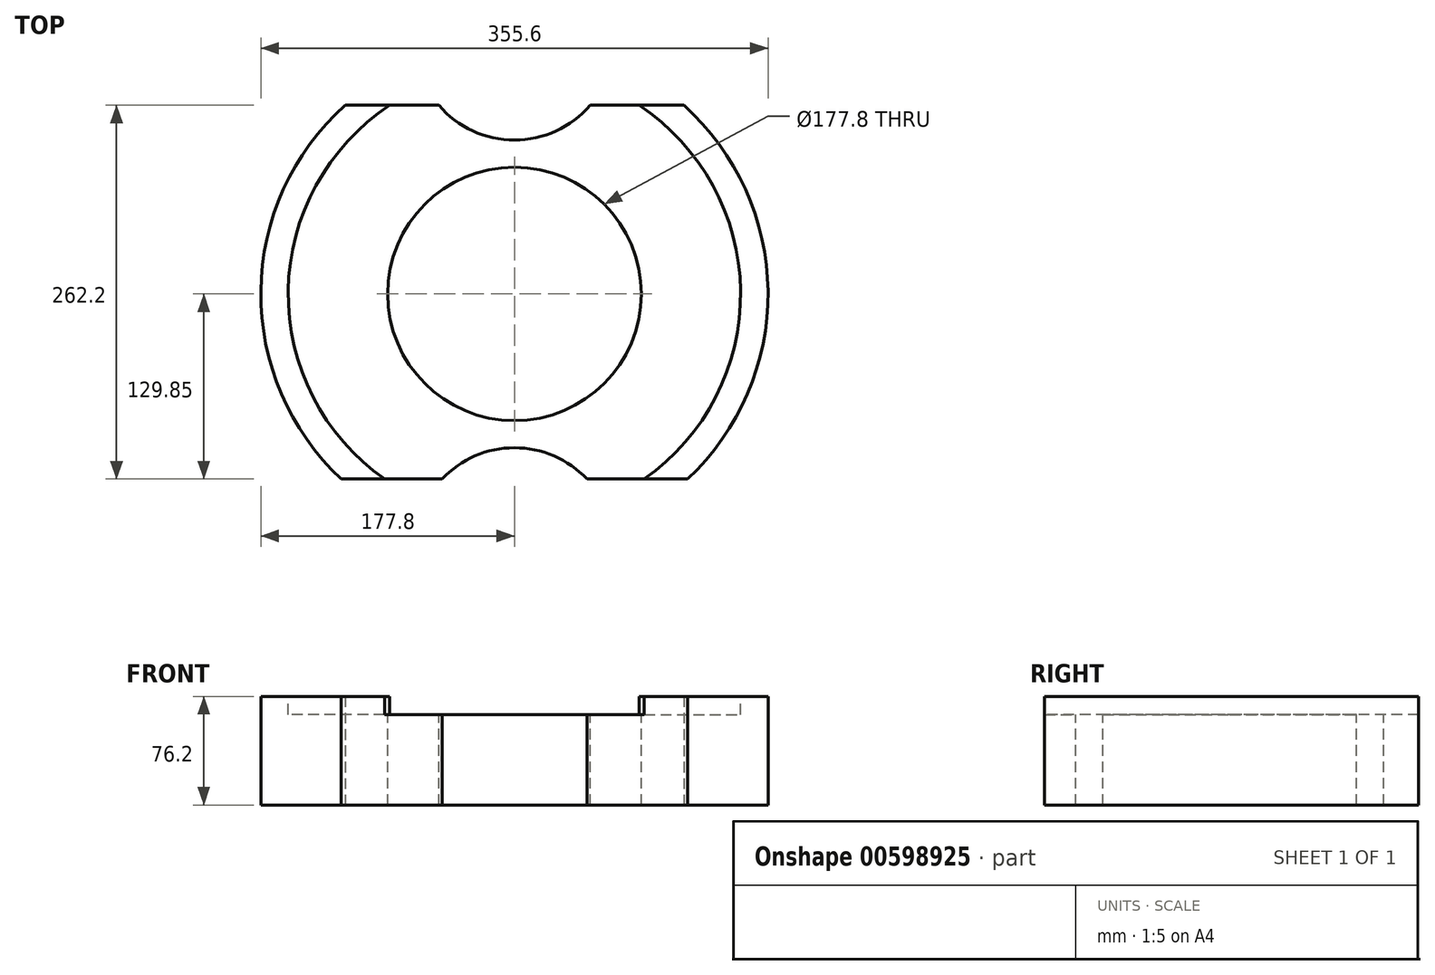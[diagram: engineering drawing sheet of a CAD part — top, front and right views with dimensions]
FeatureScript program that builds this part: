
annotation { "Feature Type Name" : "Feature", "Feature Type Description" : "" }
export const myFeature = defineFeature(function(context is Context, id is Id, definition is map)
    precondition{}
    {
        {
            var Q0;
            Q0=qCreatedBy(makeId("Top.planeOp"),FACE);
            var sketch = newSketch(context, id + "F0", { "sketchPlane" : qUnion([Q0])});
            skCircle(sketch, "E0", {"center": v(0, 0) * mm, "radius": 177.8 * mm});
            skSolve(sketch);
        }
        {
            var Q0;
            Q0 = qSketchRegion(id + "F0", true);
            extrude(context, id + "F1", {"entities" : qUnion([Q0]), "depth" : 76.2 * mm, "offsetDistance" : 25.4 * mm});
        }
        {
            var Q0;
            Q0=makeQuery(id+"F1.opExtrude","CAP_FACE",FACE,{"disambiguationData":[OSD([sQuery(id+"F0.wireOp",EDGE,"E0")])],"isStart":false});
            var sketch = newSketch(context, id + "F2", { "sketchPlane" : qUnion([Q0])});
            skCircle(sketch, "E1", {"center": v(0, 0) * mm, "radius": 88.9 * mm});
            skSolve(sketch);
        }
        {
            var Q0;
            Q0 = qSketchRegion(id + "F2", true);
            extrude(context, id + "F3", {"entities" : qUnion([Q0]), "operationType" : NewBodyOperationType.REMOVE, "oppositeDirection" : true, "depth" : 254 * mm, "offsetDistance" : 25.4 * mm});
        }
        {
            var Q0;
            Q0=makeQuery(id+"F1.opExtrude","CAP_FACE",FACE,{"disambiguationData":[OSD([sQuery(id+"F0.wireOp",EDGE,"E0")])],"isStart":false});
            var sketch = newSketch(context, id + "F4", { "sketchPlane" : qUnion([Q0])});
            skCircle(sketch, "E2", {"center": v(0, 177.8) * mm, "radius": 69.85 * mm});
            skCircle(sketch, "E3", {"center": v(0, -177.8) * mm, "radius": 69.85 * mm});
            skSolve(sketch);
        }
        {
            var Q0;
            Q0 = qSketchRegion(id + "F4", true);
            extrude(context, id + "F5", {"entities" : qUnion([Q0]), "operationType" : NewBodyOperationType.REMOVE, "oppositeDirection" : true, "depth" : 254 * mm, "offsetDistance" : 25.4 * mm});
        }
        {
            var Q0;
            Q0=makeQuery(id+"F1.opExtrude","CAP_FACE",FACE,{"disambiguationData":[OSD([sQuery(id+"F0.wireOp",EDGE,"E0")])],"isStart":false});
            var sketch = newSketch(context, id + "F6", { "sketchPlane" : qUnion([Q0])});
            skLineSegment(sketch, "E4.bottom", {"start": v(-232.14, 132.35) * mm, "end": v(229.97, 132.35) * mm});
            skLineSegment(sketch, "E4.top", {"start": v(-232.14, 178.7) * mm, "end": v(229.97, 178.7) * mm});
            skLineSegment(sketch, "E4.left", {"start": v(-232.14, 132.35) * mm, "end": v(-232.14, 178.7) * mm});
            skLineSegment(sketch, "E4.right", {"start": v(229.97, 132.35) * mm, "end": v(229.97, 178.7) * mm});
            skLineSegment(sketch, "E5.bottom", {"start": v(-232.14, -129.85) * mm, "end": v(234.31, -129.85) * mm});
            skLineSegment(sketch, "E5.top", {"start": v(-232.14, -164.08) * mm, "end": v(234.31, -164.08) * mm});
            skLineSegment(sketch, "E5.left", {"start": v(-232.14, -129.85) * mm, "end": v(-232.14, -164.08) * mm});
            skLineSegment(sketch, "E5.right", {"start": v(234.31, -129.85) * mm, "end": v(234.31, -164.08) * mm});
            skSolve(sketch);
        }
        {
            var Q0;
            Q0 = qSketchRegion(id + "F6", true);
            extrude(context, id + "F7", {"entities" : qUnion([Q0]), "operationType" : NewBodyOperationType.REMOVE, "oppositeDirection" : true, "depth" : 254 * mm, "offsetDistance" : 25.4 * mm});
        }
        {
            var Q0;
            Q0=makeQuery(id+"F1.opExtrude","CAP_FACE",FACE,{"disambiguationData":[OSD([sQuery(id+"F0.wireOp",EDGE,"E0")])],"isStart":false});
            var sketch = newSketch(context, id + "F8", { "sketchPlane" : qUnion([Q0])});
            skCircle(sketch, "E6", {"center": v(0, 0) * mm, "radius": 158.6 * mm});
            skSolve(sketch);
        }
        {
            var Q0;
            Q0 = qSketchRegion(id + "F8", true);
            extrude(context, id + "F9", {"entities" : qUnion([Q0]), "operationType" : NewBodyOperationType.REMOVE, "oppositeDirection" : true, "depth" : 12.7 * mm, "offsetDistance" : 25.4 * mm});
        }
    });
